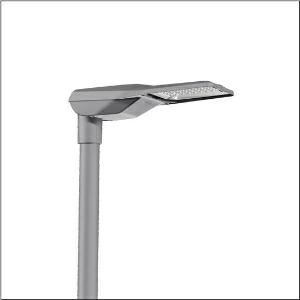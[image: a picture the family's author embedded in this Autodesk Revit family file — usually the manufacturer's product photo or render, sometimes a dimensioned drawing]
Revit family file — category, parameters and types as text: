
# Revit family: streetlight_sl_21_iq_mini___st0_8a_5xe2c31d08jb_69b6
name_source: partatom
category: Lighting Fixtures
units: mm (PartAtom-declared; Revit-internal decimal feet)

## family parameters
Cut with Voids When Loaded = No
Host = Face
Light Source = No
Part Type = Normal
Room Calculation Point = No
Round Connector Dimension = Use Diameter
Shared = No

## types (1)
- --- (1 x LED, 10820 lm, 71.6 W, 3000K)
    Apparent Load = 72 VA
    CIE Flux Codes = 41 75 97 100 100
    Color Rendering = 70
    Color Temperature = 3000K
    Default Elevation = 1800 mm
    Description = Streetlight SL 21 iQ mini, mast luminaire, primary light control with lens, of PMMA, primary optical cover: cover, of toughened safety glass, transparent, light distribution: ST0.8a, light emission: direct distribution, primary light characteristic: asymmetric, installation type: post-top, side-entry, LED, High Power LED, rated luminous flux: 10.820lm, luminous efficacy: 151lm/W, light colour: 730, colour temperature: 3000K, control: Auto-Match, Temp-Guard, Lumen-Switch, Night-Set, Smart-Wire, Light-Fading, Desk-Remote (wireless, voltage-free reading and setting of iQ features in the workshop via application-optimized NFC function/RFID function), optimised constant luminous flux control (CLO 2.0), presetting dimming linear, mains connection: 220..240V, AC, 50/60Hz, start of lifetime: 72W, end of service life: 75W, reduction: 33W, luminaire housing, of diecast aluminium, powder-coated, Siteco® metallic grey (DB 702S), corrosivity category C5 mid according to DIN EN ISO 12944, please order mast flange separately, inclination adjustable: 0°, 5°, 10°, 15°, sealing non-destructively replaceable, multi-level sealing system, length: 628mm, width: 235mm, height: 110mm, mast flange for spigot size: 42mm (side-entry): 5XC10008XM4, 60/48mm (side-entry/post-top): 5XC10108XM2, 76/60mm (side-entry/post-top): 5XC10108XM1, protection rating (complete): IP66, insulation class (complete): insulation class II (safety insulation), certification: CE, ENEC, ENEC+, VDE, impact resistance: IK09, permissible operating ambient temperature for outdoor applications: -40..+50°C, standard-compliant lighting for roads and squares, packaging unit: 1 piece

Light Distribution: ST0.8a
    Height = 110 mm
    Lamp = 1 x LED
    Lamp Light Flux = 10820 lm
    Lamp Power = 71.6 W
    Lamp count = 1
    Length = 625 mm
    Luminous efficacy = 151 lm/W
    Manufacturer = Siteco
    ModVariant = No
    Model = 5XE2C31D08JB
    Number of Poles = 1
    OnlyDefault = Yes
    Power Factor = 1
    Product Name = Streetlight SL 21 iQ mini | ST0.8a
    Product group = mast luminaire | pylon top
    ProductGroupID = 6100
    Protection Class = Protection class II
    Protection Degree = IP 66
    RLX_Detail_Level = 1
    RLX_Emergency_Light_Flux = 0 lm
    RLX_Emergency_Type = 0
    RLX_Emergency_Type_DB = No
    RlxData = <blob elided: 92237 chars, md5=f25e2015>
    Socket = socket
    Standby Power = 0 W
    System Light Flux = 10820 lm
    System Power = 72 W
    Type Comments = factory setting: luminous flux: 100 % | dim-lin: 254 | 746 mA
    Type Image = l_1003519.jpg
    URL = http://relux.com
    VarID = @adj_101887
    Voltage = 0 V
    Weight = 0.00 kg
    Width = 234 mm

## geometry (parser evidence)
native form markers: Blend x4, Sweep x11
no freeform markers — native parametric forms only
